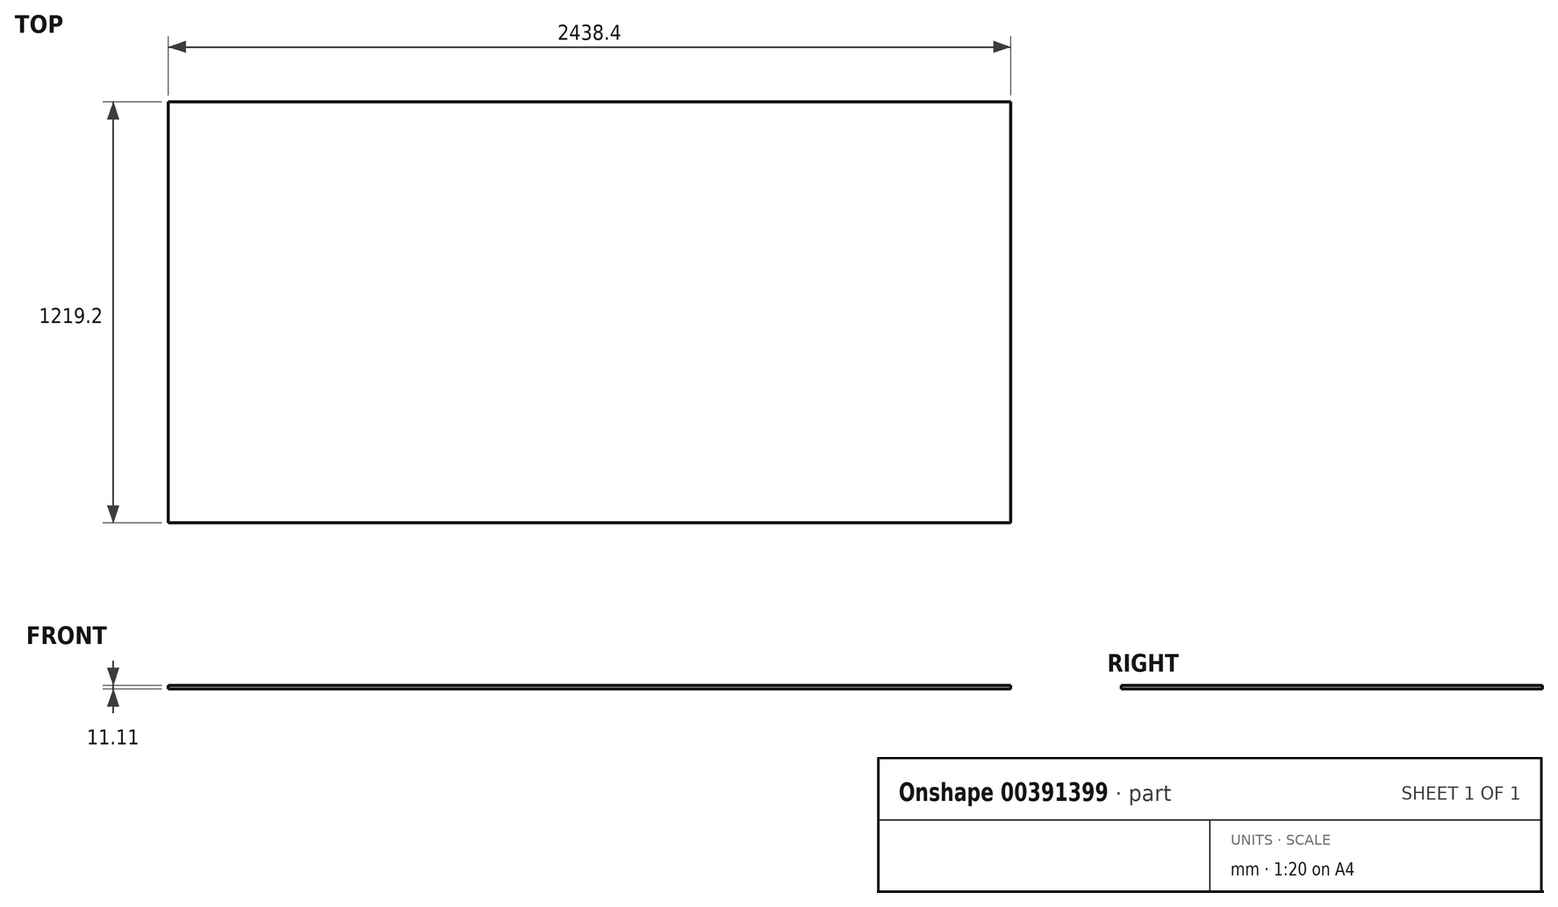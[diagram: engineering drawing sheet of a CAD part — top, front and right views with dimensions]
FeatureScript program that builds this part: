
annotation { "Feature Type Name" : "Feature", "Feature Type Description" : "" }
export const myFeature = defineFeature(function(context is Context, id is Id, definition is map)
    precondition{}
    {
        {
            var Q0;
            Q0=qCreatedBy(makeId("Top.planeOp"),FACE);
            var sketch = newSketch(context, id + "F0", { "sketchPlane" : qUnion([Q0])});
            skLineSegment(sketch, "E0.bottom", {"start": v(0, 0) * mm, "end": v(2438.4, 0) * mm});
            skLineSegment(sketch, "E0.top", {"start": v(0, 1219.2) * mm, "end": v(2438.4, 1219.2) * mm});
            skLineSegment(sketch, "E0.left", {"start": v(0, 0) * mm, "end": v(0, 1219.2) * mm});
            skLineSegment(sketch, "E0.right", {"start": v(2438.4, 0) * mm, "end": v(2438.4, 1219.2) * mm});
            skSolve(sketch);
        }
        {
            var Q0;
            Q0 = qSketchRegion(id + "F0", true);
            extrude(context, id + "F1", {"entities" : qUnion([Q0]), "depth" : 11.1 * mm});
        }
    });
